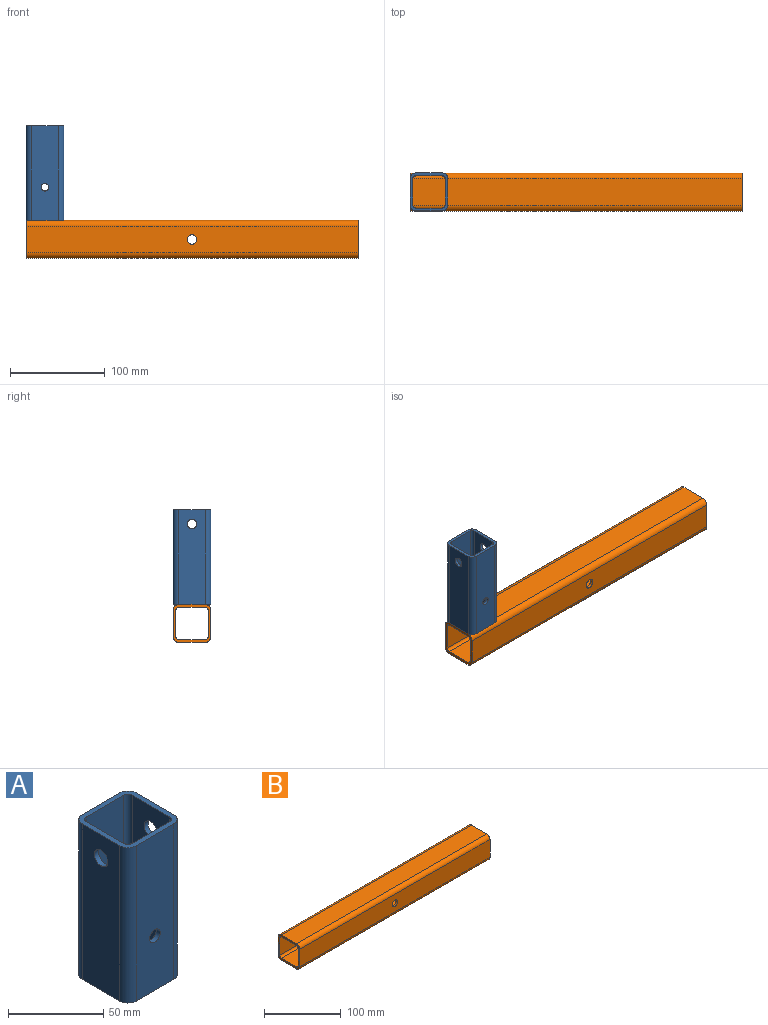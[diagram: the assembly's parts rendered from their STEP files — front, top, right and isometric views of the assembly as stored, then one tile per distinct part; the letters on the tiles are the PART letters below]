
ASSEMBLY  parts=2 mates=1
PART A: 22 faces, bbox 40x40x100 mm
  f0: plane 100x28mm, normal (0,1,0), area 2749.7mm2, adj f1,f7,f8,f9,f20
  f1: cylinder r=3mm len=100mm, axis (0,0,1), area 471.2mm2, adj f0,f2,f8,f9
  f2: plane 100x28mm, normal (1,0,0), area 2721.5mm2, adj f1,f3,f8,f9,f19
  f3: cylinder r=3mm len=100mm, axis (0,0,1), area 471.2mm2, adj f2,f4,f8,f9
  f4: plane 100x28mm, normal (0,-1,0), area 2749.7mm2, adj f3,f5,f8,f9,f21
  f5: cylinder r=3mm len=100mm, axis (0,0,1), area 471.2mm2, adj f4,f6,f8,f9
  f6: plane 100x28mm, normal (-1,0,0), area 2721.5mm2, adj f5,f7,f8,f9,f18
  f7: cylinder r=3mm len=100mm, axis (0,0,1), area 471.2mm2, adj f0,f6,f8,f9
  f8: plane 40x40mm, normal (0,0,-1), area 420.8mm2, adj f0,f1,f2,f3,f4,f5,f6,f7
  f9: plane 40x40mm, normal (0,0,1), area 420.8mm2, adj f0,f1,f2,f3,f4,f5,f6,f7
  f10: plane 100x28mm, normal (0,1,0), area 2749.7mm2, adj f8,f9,f11,f17,f21
  f11: cylinder r=6mm len=100mm, axis (0,0,1), area 942.5mm2, adj f8,f9,f10,f12
  f12: plane 100x28mm, normal (-1,0,0), area 2721.5mm2, adj f8,f9,f11,f13,f19
  f13: cylinder r=6mm len=100mm, axis (0,0,1), area 942.5mm2, adj f8,f9,f12,f14
  f14: plane 100x28mm, normal (0,-1,0), area 2749.7mm2, adj f8,f9,f13,f15,f20
  f15: cylinder r=6mm len=100mm, axis (0,0,1), area 942.5mm2, adj f8,f9,f14,f16
  f16: plane 100x28mm, normal (1,0,0), area 2721.5mm2, adj f8,f9,f15,f17,f18
  f17: cylinder r=6mm len=100mm, axis (0,0,1), area 942.5mm2, adj f8,f9,f10,f16
  f18: cylinder r=5mm len=10mm, axis (1,0,0), area 94.2mm2, adj f6,f16
  f19: cylinder r=5mm len=10mm, axis (1,0,0), area 94.2mm2, adj f2,f12
  f20: cylinder r=4mm len=8mm, axis (0,-1,0), area 75.4mm2, adj f0,f14
  f21: cylinder r=4mm len=8mm, axis (0,-1,0), area 75.4mm2, adj f4,f10
PART B: 20 faces, bbox 350x40x40 mm
  f0: plane 350x28mm, normal (0,0,-1), area 9800mm2, adj f1,f7,f8,f9
  f1: cylinder r=3mm len=350mm, axis (-1,0,0), area 1649.3mm2, adj f0,f2,f8,f9
  f2: plane 350x28mm, normal (0,1,0), area 9721.5mm2, adj f1,f3,f8,f9,f19
  f3: cylinder r=3mm len=350mm, axis (-1,0,0), area 1649.3mm2, adj f2,f4,f8,f9
  f4: plane 350x28mm, normal (0,0,1), area 9800mm2, adj f3,f5,f8,f9
  f5: cylinder r=3mm len=350mm, axis (-1,0,0), area 1649.3mm2, adj f4,f6,f8,f9
  f6: plane 350x28mm, normal (0,-1,0), area 9721.5mm2, adj f5,f7,f8,f9,f18
  f7: cylinder r=3mm len=350mm, axis (-1,0,0), area 1649.3mm2, adj f0,f6,f8,f9
  f8: plane 40x40mm, normal (1,0,0), area 420.8mm2, adj f0,f1,f2,f3,f4,f5,f6,f7
  f9: plane 40x40mm, normal (-1,0,0), area 420.8mm2, adj f0,f1,f2,f3,f4,f5,f6,f7
  f10: plane 350x28mm, normal (0,0,-1), area 9800mm2, adj f8,f9,f11,f17
  f11: cylinder r=6mm len=350mm, axis (-1,0,0), area 3298.7mm2, adj f8,f9,f10,f12
  f12: plane 350x28mm, normal (0,-1,0), area 9721.5mm2, adj f8,f9,f11,f13,f19
  f13: cylinder r=6mm len=350mm, axis (-1,0,0), area 3298.7mm2, adj f8,f9,f12,f14
  f14: plane 350x28mm, normal (0,0,1), area 9800mm2, adj f8,f9,f13,f15
  f15: cylinder r=6mm len=350mm, axis (-1,0,0), area 3298.7mm2, adj f8,f9,f14,f16
  f16: plane 350x28mm, normal (0,1,0), area 9721.5mm2, adj f8,f9,f15,f17,f18
  f17: cylinder r=6mm len=350mm, axis (-1,0,0), area 3298.7mm2, adj f8,f9,f10,f16
  f18: cylinder r=5mm len=10mm, axis (0,-1,0), area 94.2mm2, adj f6,f16
  f19: cylinder r=5mm len=10mm, axis (0,-1,0), area 94.2mm2, adj f2,f12
PLACE A t=(-330,0,20)mm
PLACE B at identity fixed
MATE fastened A.f8 <-> B.f14  axis (0,0,-1) through (-350,0,20)mm
